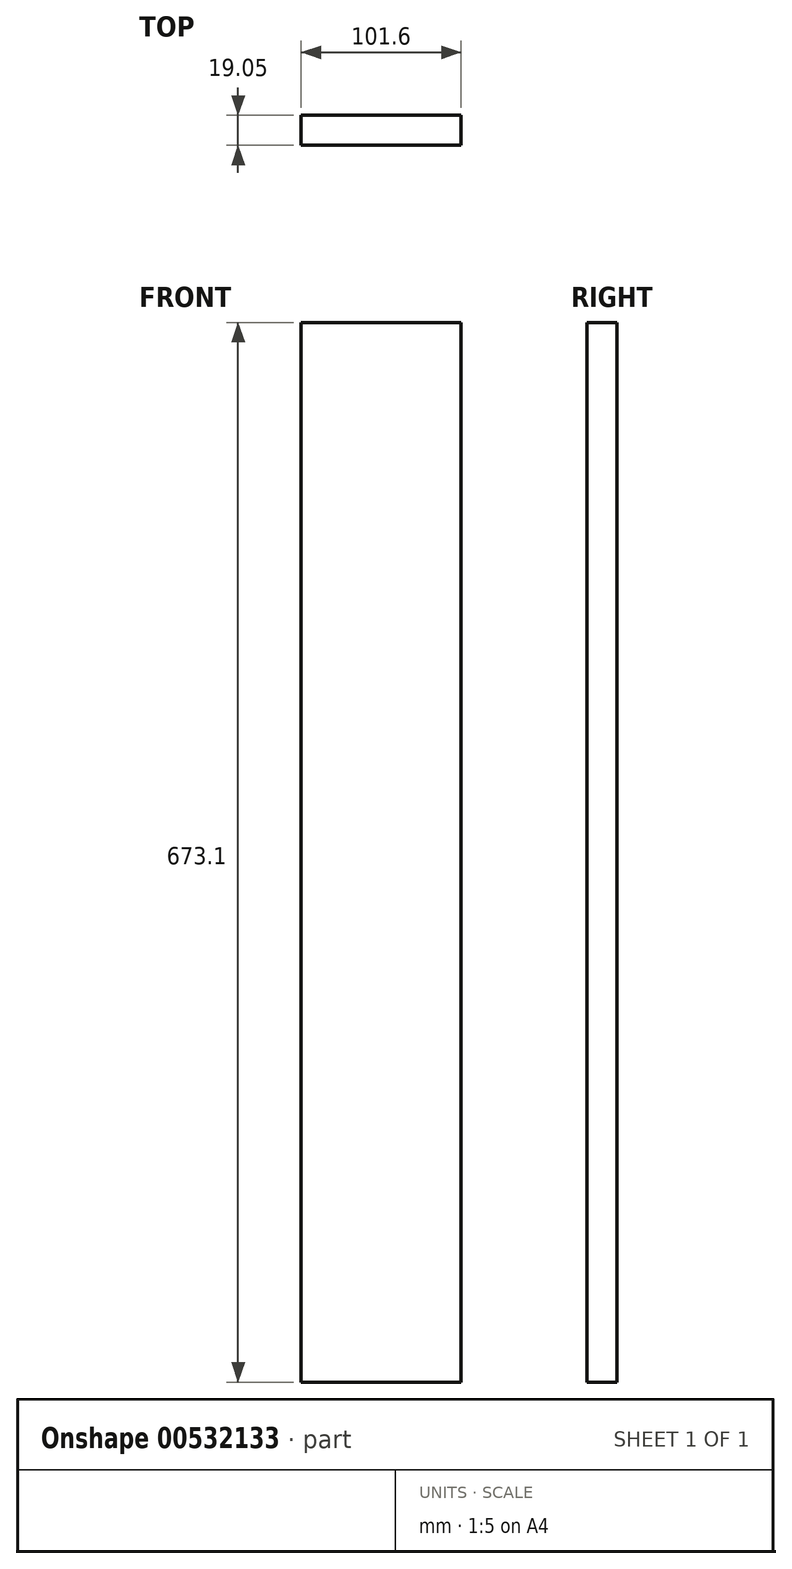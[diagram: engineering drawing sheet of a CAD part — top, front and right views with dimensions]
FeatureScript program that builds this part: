
annotation { "Feature Type Name" : "Feature", "Feature Type Description" : "" }
export const myFeature = defineFeature(function(context is Context, id is Id, definition is map)
    precondition{}
    {
        {
            var Q0;
            Q0=qCreatedBy(makeId("Front.planeOp"),FACE);
            var sketch = newSketch(context, id + "F0", { "sketchPlane" : qUnion([Q0])});
            skLineSegment(sketch, "E0.bottom", {"start": v(50.8, -336.55) * mm, "end": v(-50.8, -336.55) * mm});
            skLineSegment(sketch, "E0.top", {"start": v(50.8, 336.55) * mm, "end": v(-50.8, 336.55) * mm});
            skLineSegment(sketch, "E0.left", {"start": v(50.8, -336.55) * mm, "end": v(50.8, 336.55) * mm});
            skLineSegment(sketch, "E0.right", {"start": v(-50.8, -336.55) * mm, "end": v(-50.8, 336.55) * mm});
            skPoint(sketch, "E0.middle", {"position": v(0, 0) * mm});
            skSolve(sketch);
        }
        {
            var Q0;
            Q0 = qSketchRegion(id + "F0", true);
            extrude(context, id + "F1", {"entities" : qUnion([Q0]), "depth" : 19.05 * mm, "offsetDistance" : 25.4 * mm});
        }
    });
